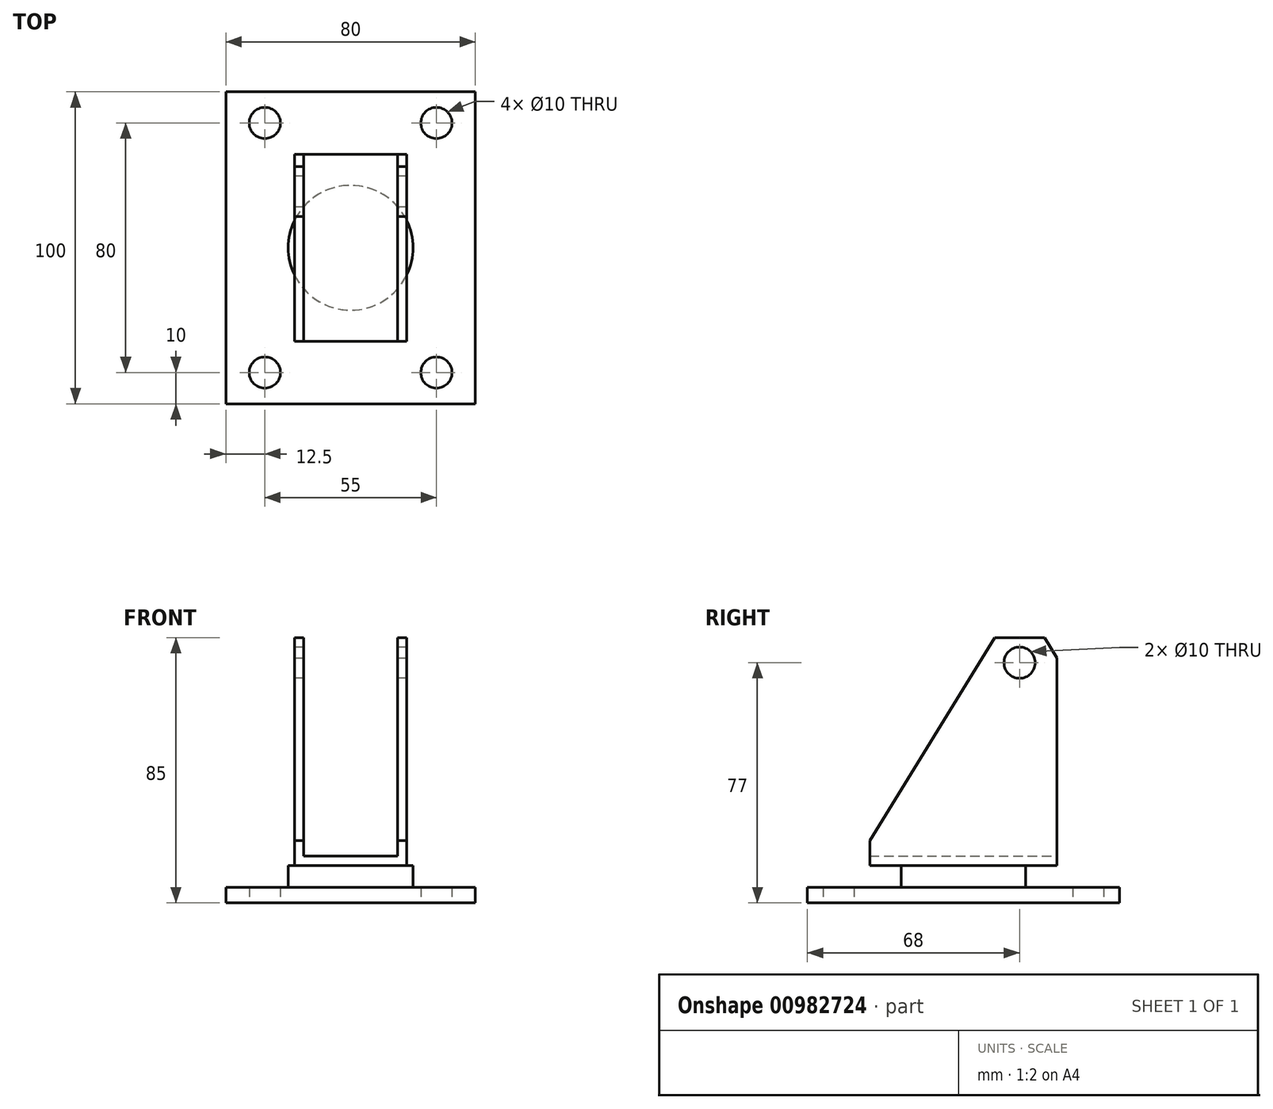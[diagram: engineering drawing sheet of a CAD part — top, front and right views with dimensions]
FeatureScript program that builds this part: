
annotation { "Feature Type Name" : "Feature", "Feature Type Description" : "" }
export const myFeature = defineFeature(function(context is Context, id is Id, definition is map)
    precondition{}
    {
        {
            var Q0;
            Q0=qCreatedBy(makeId("Top.planeOp"),FACE);
            var sketch = newSketch(context, id + "F0", { "sketchPlane" : qUnion([Q0])});
            skLineSegment(sketch, "E0.bottom", {"start": v(40, -50) * mm, "end": v(-40, -50) * mm});
            skLineSegment(sketch, "E0.top", {"start": v(40, 50) * mm, "end": v(-40, 50) * mm});
            skLineSegment(sketch, "E0.left", {"start": v(40, -50) * mm, "end": v(40, 50) * mm});
            skLineSegment(sketch, "E0.right", {"start": v(-40, -50) * mm, "end": v(-40, 50) * mm});
            skPoint(sketch, "E0.middle", {"position": v(0, 0) * mm});
            skCircle(sketch, "E1", {"center": v(-27.5, 40) * mm, "radius": 5 * mm});
            skCircle(sketch, "E2.MirrorC", {"center": v(27.5, 40) * mm, "radius": 5 * mm});
            skCircle(sketch, "E3.MirrorC", {"center": v(-27.5, -40) * mm, "radius": 5 * mm});
            skCircle(sketch, "E4.MirrorC", {"center": v(27.5, -40) * mm, "radius": 5 * mm});
            skCircle(sketch, "E5", {"center": v(0, 0) * mm, "radius": 20 * mm});
            skSolve(sketch);
        }
        {
            var Q0;
            Q0=makeQuery(id+"F0.imprint","IMPRINT",FACE,{"disambiguationData":[TD([[makeQuery(id+"F0.imprint","IMPRINT",EDGE,{"derivedFrom":sQuery(id+"F0.wireOp",EDGE,"E0.bottom")}),-1.0]])]});
            var Q1;
            Q1=makeQuery(id+"F0.imprint","IMPRINT",FACE,{"disambiguationData":[TD([[makeQuery(id+"F0.imprint","IMPRINT",EDGE,{"derivedFrom":sQuery(id+"F0.wireOp",EDGE,"E5")}),1.0]])]});
            extrude(context, id + "F1", {"entities" : qUnion([Q0, Q1]), "depth" : 5 * mm, "offsetDistance" : 25 * mm});
        }
        {
            var Q0;
            Q0=makeQuery(id+"F0.imprint","IMPRINT",FACE,{"disambiguationData":[TD([[makeQuery(id+"F0.imprint","IMPRINT",EDGE,{"derivedFrom":sQuery(id+"F0.wireOp",EDGE,"E5")}),1.0]])]});
            extrude(context, id + "F2", {"entities" : qUnion([Q0]), "operationType" : NewBodyOperationType.ADD, "depth" : 12 * mm, "offsetDistance" : 25 * mm});
        }
        {
            var Q0;
            Q0=makeQuery(id+"F2.opExtrude","CAP_FACE",FACE,{"disambiguationData":[OSD([sQuery(id+"F0.wireOp",EDGE,"E5")])],"isStart":false});
            var sketch = newSketch(context, id + "F3", { "sketchPlane" : qUnion([Q0])});
            skLineSegment(sketch, "E6.bottom", {"start": v(18, -30) * mm, "end": v(-18, -30) * mm});
            skLineSegment(sketch, "E6.top", {"start": v(18, 30) * mm, "end": v(-18, 30) * mm});
            skLineSegment(sketch, "E6.left", {"start": v(18, -30) * mm, "end": v(18, 30) * mm});
            skLineSegment(sketch, "E6.right", {"start": v(-18, -30) * mm, "end": v(-18, 30) * mm});
            skPoint(sketch, "E6.middle", {"position": v(0, 0) * mm});
            skSolve(sketch);
        }
        {
            var Q0;
            {var subQ0=sQuery(id+"F3.wireOp",EDGE,"E6.bottom");Q0=makeQuery(id+"F3.imprint","IMPRINT",FACE,{"disambiguationData":[TD([[makeQuery(id+"F3.imprint","IMPRINT",EDGE,{"derivedFrom":subQ0}),-1.0]])]});}
            var Q1;
            {var subQ0=sQuery(id+"F3.wireOp",EDGE,"E6.left");var subQ1=makeQuery(id+"F2.opExtrude","CAP_EDGE",EDGE,{"disambiguationData":[OSD([sQuery(id+"F0.wireOp",EDGE,"E5")])],"isStart":false});var subQ2=makeQuery(id+"F3.imprint","INTERSECT",VERTEX,{"disambiguationData":[OD(0.0)],"derivedFrom":[subQ1,subQ0]});Q1=makeQuery(id+"F3.imprint","IMPRINT",FACE,{"disambiguationData":[TD([[makeQuery(id+"F3.imprint","IMPRINT",EDGE,{"disambiguationData":[TD([[subQ2,-1.0]])],"derivedFrom":subQ0}),1.0]])]});}
            var Q2;
            {var subQ0=sQuery(id+"F3.wireOp",EDGE,"E6.top");Q2=makeQuery(id+"F3.imprint","IMPRINT",FACE,{"disambiguationData":[TD([[makeQuery(id+"F3.imprint","IMPRINT",EDGE,{"derivedFrom":subQ0}),1.0]])]});}
            extrude(context, id + "F4", {"entities" : qUnion([Q0, Q1, Q2]), "operationType" : NewBodyOperationType.ADD, "depth" : 3 * mm, "offsetDistance" : 25 * mm});
        }
        {
            var Q0;
            Q0=makeQuery(id+"F4.opExtrude","CAP_FACE",FACE,{"disambiguationData":[OSD([sQuery(id+"F3.wireOp",EDGE,"E6.bottom"),sQuery(id+"F3.wireOp",EDGE,"E6.top"),sQuery(id+"F3.wireOp",EDGE,"E6.left"),sQuery(id+"F3.wireOp",EDGE,"E6.right")])],"isStart":false});
            var sketch = newSketch(context, id + "F5", { "sketchPlane" : qUnion([Q0])});
            skLineSegment(sketch, "E7.bottom", {"start": v(-18, 30) * mm, "end": v(-15, 30) * mm});
            skLineSegment(sketch, "E7.top", {"start": v(-18, -30) * mm, "end": v(-15, -30) * mm});
            skLineSegment(sketch, "E7.left", {"start": v(-18, 30) * mm, "end": v(-18, -30) * mm});
            skLineSegment(sketch, "E7.right", {"start": v(-15, 30) * mm, "end": v(-15, -30) * mm});
            skLineSegment(sketch, "E8.bottom", {"start": v(18, -30) * mm, "end": v(18, -30) * mm});
            skLineSegment(sketch, "E8.top", {"start": v(18, 30) * mm, "end": v(18, 30) * mm});
            skLineSegment(sketch, "E8.left", {"start": v(18, -30) * mm, "end": v(18, 30) * mm});
            skLineSegment(sketch, "E8.right", {"start": v(18, -30) * mm, "end": v(18, 30) * mm});
            skLineSegment(sketch, "E9.bottom", {"start": v(18, -30) * mm, "end": v(15, -30) * mm});
            skLineSegment(sketch, "E9.top", {"start": v(18, 30) * mm, "end": v(15, 30) * mm});
            skLineSegment(sketch, "E9.right", {"start": v(15, -30) * mm, "end": v(15, 30) * mm});
            skSolve(sketch);
        }
        {
            var Q0;
            Q0=makeQuery(id+"F5.imprint","IMPRINT",FACE,{"disambiguationData":[TD([[makeQuery(id+"F5.imprint","IMPRINT",EDGE,{"derivedFrom":sQuery(id+"F5.wireOp",EDGE,"E7.bottom")}),1.0]])]});
            var Q1;
            Q1=makeQuery(id+"F5.imprint","IMPRINT",FACE,{"disambiguationData":[TD([[makeQuery(id+"F5.imprint","IMPRINT",EDGE,{"derivedFrom":sQuery(id+"F5.wireOp",EDGE,"E9.bottom")}),-1.0]])]});
            extrude(context, id + "F6", {"entities" : qUnion([Q0, Q1]), "operationType" : NewBodyOperationType.ADD, "depth" : 70 * mm, "offsetDistance" : 25 * mm});
        }
        {
            var Q0;
            Q0=makeQuery(id+"F6.opExtrude","CAP_EDGE",EDGE,{"disambiguationData":[OSD([sQuery(id+"F5.wireOp",EDGE,"E9.bottom")])],"isStart":false});
            var Q1;
            Q1=makeQuery(id+"F6.opExtrude","CAP_EDGE",EDGE,{"disambiguationData":[OSD([sQuery(id+"F5.wireOp",EDGE,"E7.top")])],"isStart":false});
            chamfer(context, id + "F7", {"entities" : qUnion([Q0, Q1]), "chamferType" : ChamferType.TWO_OFFSETS, "width1" : 65 * mm, "oppositeDirection" : false, "width2" : 40 * mm, "tangentPropagation" : true});
        }
        {
            var Q0;
            Q0=makeQuery(id+"F6.opExtrude","CAP_EDGE",EDGE,{"disambiguationData":[OSD([sQuery(id+"F5.wireOp",EDGE,"E9.top")])],"isStart":false});
            var Q1;
            Q1=makeQuery(id+"F6.opExtrude","CAP_EDGE",EDGE,{"disambiguationData":[OSD([sQuery(id+"F5.wireOp",EDGE,"E7.bottom")])],"isStart":false});
            chamfer(context, id + "F8", {"entities" : qUnion([Q0, Q1]), "chamferType" : ChamferType.TWO_OFFSETS, "width1" : 4 * mm, "oppositeDirection" : false, "width2" : 6.5 * mm, "tangentPropagation" : true});
        }
        {
            var Q0;
            Q0=makeQuery(id+"F6.boolean.opBoolean","MERGE",FACE,{"derivedFrom":[makeQuery(id+"F4.opExtrude","SWEPT_FACE",FACE,{"disambiguationData":[OSD([sQuery(id+"F3.wireOp",EDGE,"E6.right")])]}),makeQuery(id+"F6.opExtrude","SWEPT_FACE",FACE,{"disambiguationData":[OSD([sQuery(id+"F5.wireOp",EDGE,"E7.left")])]})]});
            var sketch = newSketch(context, id + "F9", { "sketchPlane" : qUnion([Q0])});
            skCircle(sketch, "E10", {"center": v(-18, 77) * mm, "radius": 5 * mm});
            skPoint(sketch, "E10.centerSnap0", {"position": v(-18, 85) * mm});
            skSolve(sketch);
        }
        {
            var Q0;
            Q0=makeQuery(id+"F9.imprint","IMPRINT",FACE,{"disambiguationData":[TD([[makeQuery(id+"F9.imprint","IMPRINT",EDGE,{"derivedFrom":sQuery(id+"F9.wireOp",EDGE,"E10")}),1.0]])]});
            extrude(context, id + "F10", {"entities" : qUnion([Q0]), "operationType" : NewBodyOperationType.REMOVE, "oppositeDirection" : true, "depth" : 60 * mm, "offsetDistance" : 25 * mm});
        }
    });
